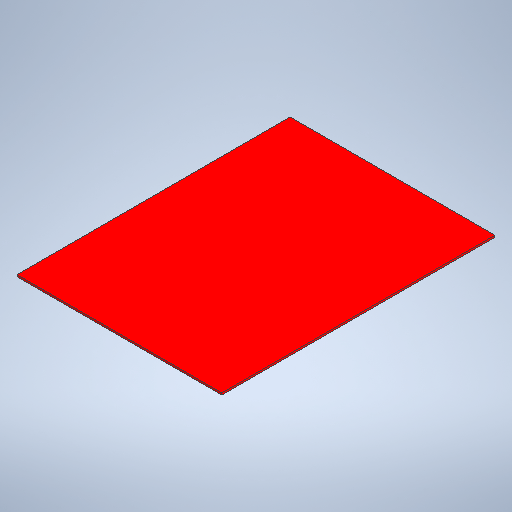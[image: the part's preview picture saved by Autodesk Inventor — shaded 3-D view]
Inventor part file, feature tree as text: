
AUTODESK INVENTOR PART (.ipt)
format: ipt  version: 2025.2 (Build 292293000, 293)  size: 232,448 bytes
history: native  units: mm
features: extrude x1, sketch x1
ambient origin geometry x8: Origin, YZ Plane, XZ Plane, XY Plane, X Axis, Y Axis, Z Axis, Center Point
bodies: Solid1 (feature_tree)
feature tree (2):
  extrude  "Extrusion1"  Depth=114.3mm
  sketch  "Sketch1"  dims[d5=1.0mm d6=0.0mm d7=114.3mm d8=152.4mm]
